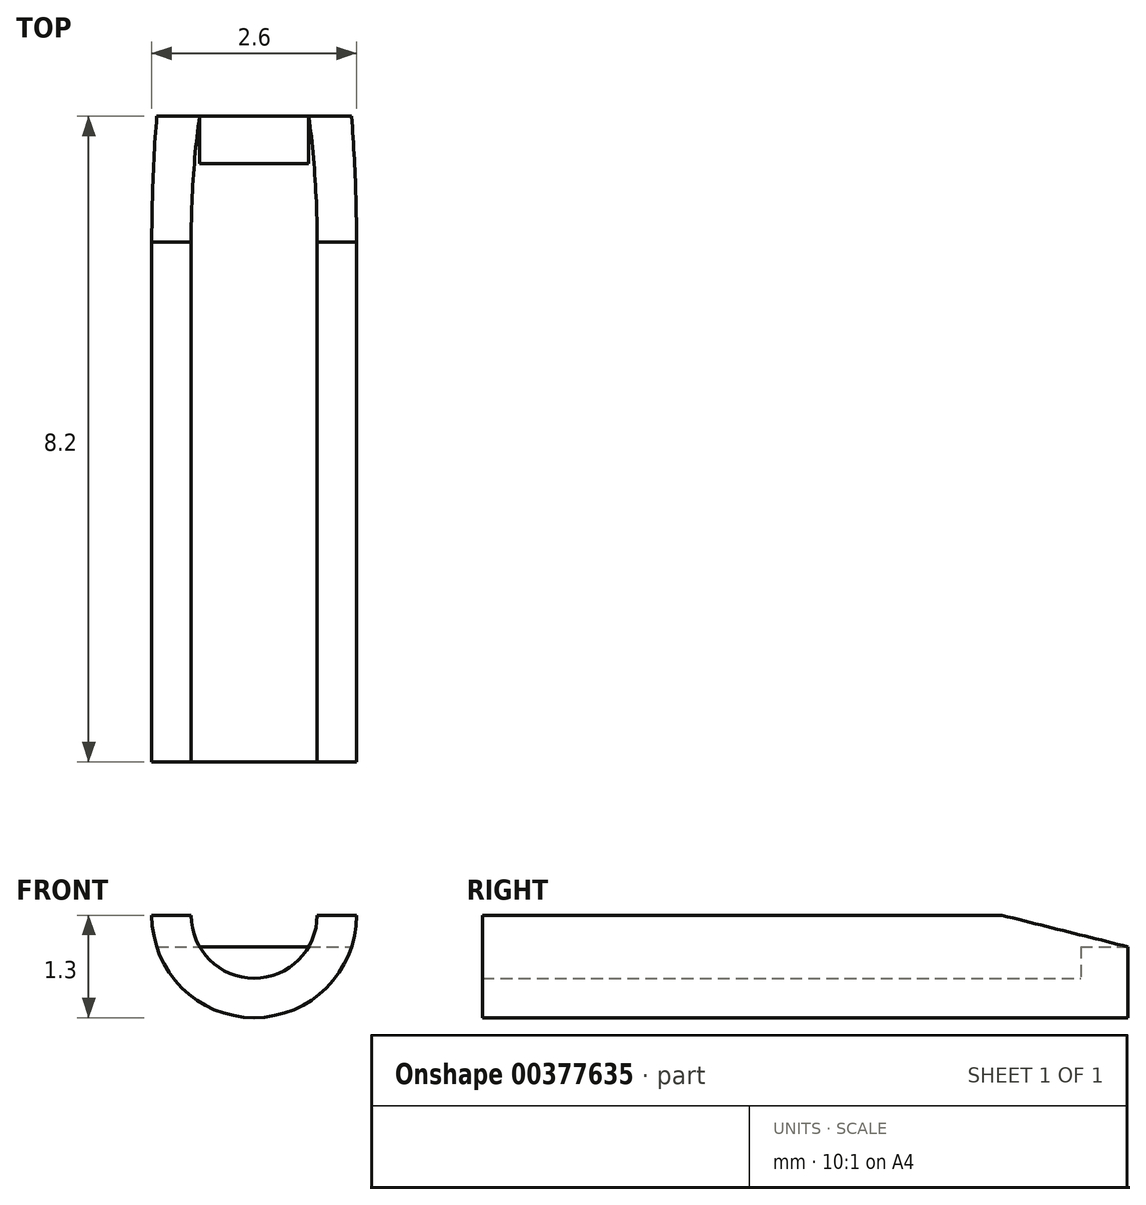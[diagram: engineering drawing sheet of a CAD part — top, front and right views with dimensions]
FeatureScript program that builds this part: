
annotation { "Feature Type Name" : "Feature", "Feature Type Description" : "" }
export const myFeature = defineFeature(function(context is Context, id is Id, definition is map)
    precondition{}
    {
        {
            var Q0;
            Q0=qCreatedBy(makeId("Front.planeOp"),FACE);
            var sketch = newSketch(context, id + "F0", { "sketchPlane" : qUnion([Q0])});
            skArc(sketch, "E0", {"start": v(0.8, 0) * mm, "mid": v(0, -0.8) * mm, "end": v(-0.8, 0) * mm});
            skArc(sketch, "E1", {"start": v(1.3, 0) * mm, "mid": v(0, -1.3) * mm, "end": v(-1.3, 0) * mm});
            skLineSegment(sketch, "E2", {"start": v(-1.3, 0) * mm, "end": v(-0.8, 0) * mm});
            skLineSegment(sketch, "E3", {"start": v(0.8, 0) * mm, "end": v(1.3, 0) * mm});
            skSolve(sketch);
        }
        {
            var Q0;
            Q0=qSketchRegion(id+"F0",true);
            extrude(context, id + "F1", {"entities" : qUnion([Q0]), "depth" : 8.2 * mm});
        }
        {
            var Q0;
            Q0=qCreatedBy(makeId("Right.planeOp"),FACE);
            var sketch = newSketch(context, id + "F2", { "sketchPlane" : qUnion([Q0])});
            skLineSegment(sketch, "E4", {"start": v(0, -0.4) * mm, "end": v(-1.6, 0) * mm});
            skLineSegment(sketch, "E5", {"start": v(-1.6, 0) * mm, "end": v(0, 0) * mm});
            skLineSegment(sketch, "E6", {"start": v(0, -0.4) * mm, "end": v(0, 0) * mm});
            skSolve(sketch);
        }
        {
            var Q0;
            Q0=qSketchRegion(id+"F2",true);
            extrude(context, id + "F3", {"entities" : qUnion([Q0]), "operationType" : NewBodyOperationType.REMOVE, "endBound" : BoundingType.SYMMETRIC, "oppositeDirection" : true, "depth" : 30 * mm});
        }
        {
            var Q0;
            Q0=makeQuery(id+"F1.opExtrude","CAP_FACE",FACE,{"disambiguationData":[OSD([sQuery(id+"F0.wireOp",EDGE,"E0"),sQuery(id+"F0.wireOp",EDGE,"E1"),sQuery(id+"F0.wireOp",EDGE,"E2"),sQuery(id+"F0.wireOp",EDGE,"E3")])],"isStart":true});
            var sketch = newSketch(context, id + "F4", { "sketchPlane" : qUnion([Q0])});
            skArc(sketch, "E7.0", {"start": v(-0.7, -0.4) * mm, "mid": v(0, -0.8) * mm, "end": v(0.7, -0.4) * mm});
            skLineSegment(sketch, "E8", {"start": v(-0.7, -0.4) * mm, "end": v(0.7, -0.4) * mm});
            skSolve(sketch);
        }
        {
            var Q0;
            Q0=qSketchRegion(id+"F4",true);
            extrude(context, id + "F5", {"entities" : qUnion([Q0]), "operationType" : NewBodyOperationType.ADD, "oppositeDirection" : true, "depth" : 0.6 * mm});
        }
    });
